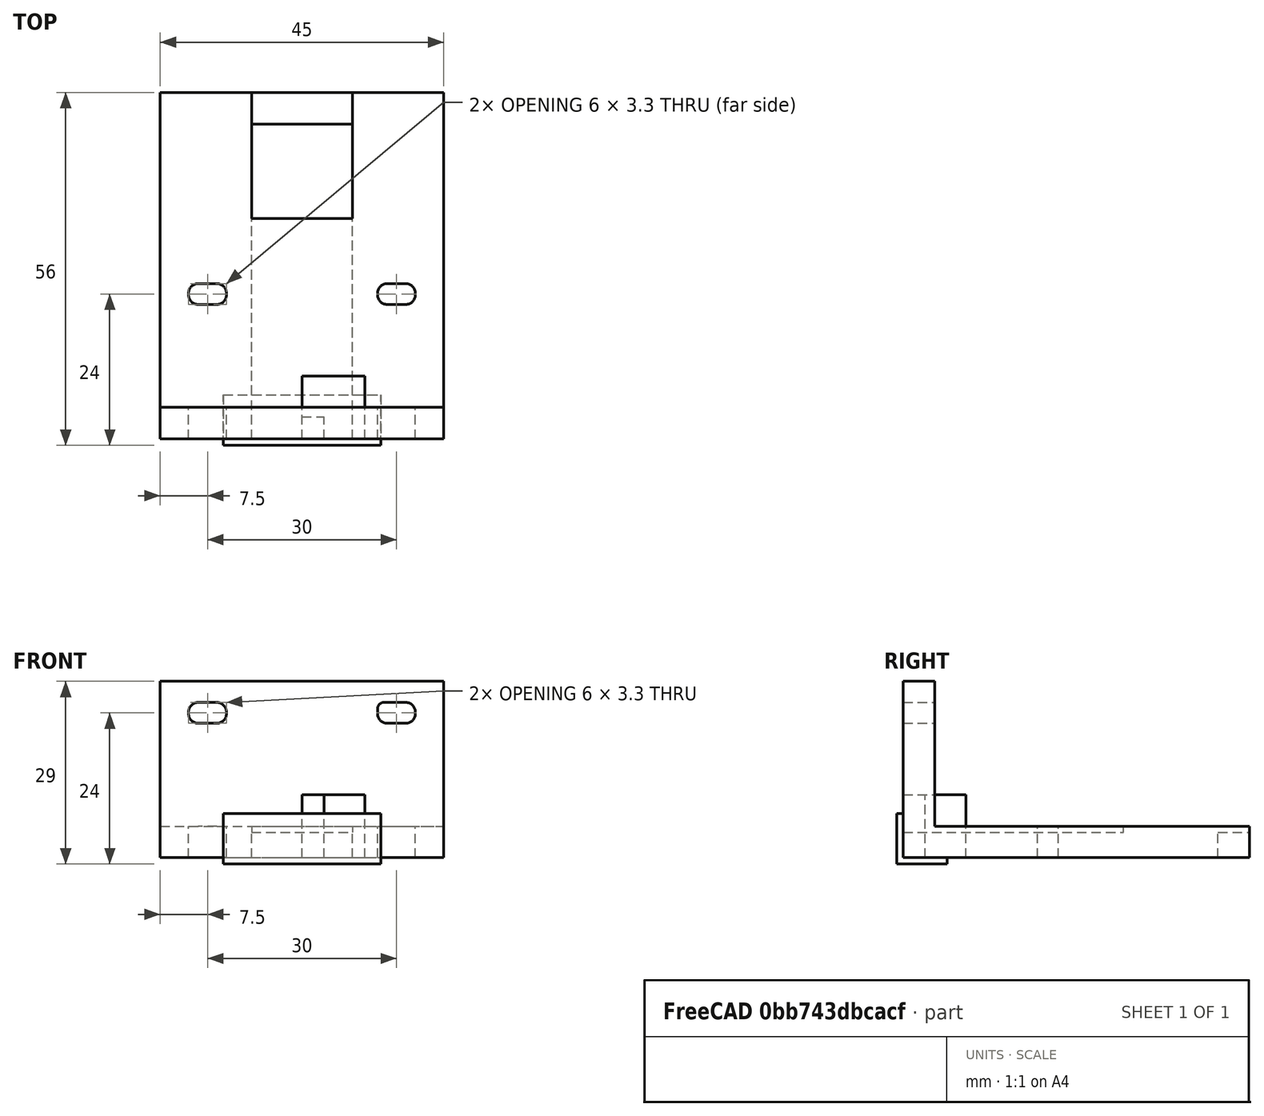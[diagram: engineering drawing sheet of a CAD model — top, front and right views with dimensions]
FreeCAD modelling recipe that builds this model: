
FCSTD DOCUMENT  (FreeCAD 0.17R13522 (Git))
Label: 蓝牙支架
License: All rights reserved
LicenseURL: http://en.wikipedia.org/wiki/All_rights_reserved
objects: Part::Box×11, Part::Fillet×4, App::DocumentObjectGroup×2, Part::MultiFuse×2, App::MeasureDistance×2, Part::Cut×1, Part::Feature×1
note: 19 computed .brp shape members not serialized (recipe doc carries the construction recipe); baked Part::Feature solids carry a one-line shape summary decoded from their .brp

FEATURE [Part::Box] Box007  label="蓝牙开孔004"
  AttacherType = Attacher::AttachEngine3D
  Height = 8
  Length = 25
  Placement = pos=(-12.5,-1,-1) rot=(0,0,1;0rad)
  Width = 8
FEATURE [Part::Box] Box  label="立方体"
  AttacherType = Attacher::AttachEngine3D
  Height = 28
  Length = 45
  Placement = pos=(-22.5,0,0) rot=(0,0,1;0rad)
  Width = 55
FEATURE [Part::Box] Box008  label="立方体001"
  AttacherType = Attacher::AttachEngine3D
  Height = 10
  Length = 3.5
  Width = 3.5
FEATURE [Part::Box] Box009  label="模块"
  AttacherType = Attacher::AttachEngine3D
  Height = 4
  Length = 16
  Placement = pos=(-8,0,0) rot=(0,0,1;0rad)
  Width = 50
FEATURE [Part::Box] Box011  label="立方体003"
  AttacherType = Attacher::AttachEngine3D
  Height = 10
  Length = 10
  Width = 10
FEATURE [Part::Box] Box012  label="立方体004"
  AttacherType = Attacher::AttachEngine3D
  Height = 6
  Length = 16
  Placement = pos=(-8,35,4) rot=(0,0,1;0rad)
  Width = 25
FEATURE [Part::Box] Box013  label="立方体005"
  AttacherType = Attacher::AttachEngine3D
  Height = 10
  Length = 6
  Placement = pos=(12,21.35,0) rot=(0,0,1;0rad)
  Width = 3.3
FEATURE [App::DocumentObjectGroup] ___
FEATURE [Part::Box] Box014  label="立方体006"
  AttacherType = Attacher::AttachEngine3D
  Height = 10
  Length = 6
  Placement = pos=(-18,21.35,0) rot=(0,0,1;0rad)
  Width = 3.3
FEATURE [App::DocumentObjectGroup] ___001
FEATURE [Part::Box] Box015  label="立方体007"
  AttacherType = Attacher::AttachEngine3D
  Height = 3.3
  Length = 6
  Placement = pos=(12,0,21.35) rot=(0,0,1;0rad)
  Width = 10
FEATURE [Part::Box] Box016  label="立方体008"
  AttacherType = Attacher::AttachEngine3D
  Height = 3.3
  Length = 6
  Placement = pos=(-18,0,21.35) rot=(0,0,1;0rad)
  Width = 10
FEATURE [Part::Box] Box017  label="立方体009"
  AttacherType = Attacher::AttachEngine3D
  Height = 23
  Length = 45
  Placement = pos=(-22.5,5,5) rot=(0,0,1;0rad)
  Width = 50
FEATURE [Part::MultiFuse] Fusion  label="整体"
  Shapes = -> [Box007,Box]
FEATURE [Part::Fillet] Fillet
  Base = -> Box014
  Edges = 4 edges r=1.5: [Edge1,Edge3,Edge5,Edge7]
FEATURE [Part::Fillet] Fillet001
  Base = -> Box016
  Edges = 4 edges r=1.5: [Edge2,Edge4,Edge6,Edge8]
FEATURE [Part::Fillet] Fillet002
  Base = -> Box015
  Edges = 4 edges: [Edge2 r=1,Edge4 r=1.5,Edge6 r=1.5,Edge8 r=1.5]
FEATURE [Part::Fillet] Fillet003
  Base = -> Box013
  Edges = 4 edges r=1.5: [Edge1,Edge3,Edge5,Edge7]
FEATURE [Part::MultiFuse] Fusion001
  Shapes = -> [Box009,Fillet001,Fillet003,Fillet002,Box012,Box017,Fillet]
FEATURE [Part::Cut] Cut
  Base = -> Fusion
  Tool = -> Fusion001
FEATURE [Part::Feature] Cut001
  shape: bbox 45 x 56 x 29 mm, 56 faces (baked)
FEATURE [App::MeasureDistance] Distance  label="Distance: 7.01 mm"
  Distance = 7.00954
  P1 = (-22.5,7,18.9447)
  P2 = (-22.5,0,18.5793)
FEATURE [App::MeasureDistance] Distance001  label="Distance: 8.07 mm"
  Distance = 8.07152
  P1 = (-22.5,20.4882,8.03904)
  P2 = (-22.5,19.7648,0)
